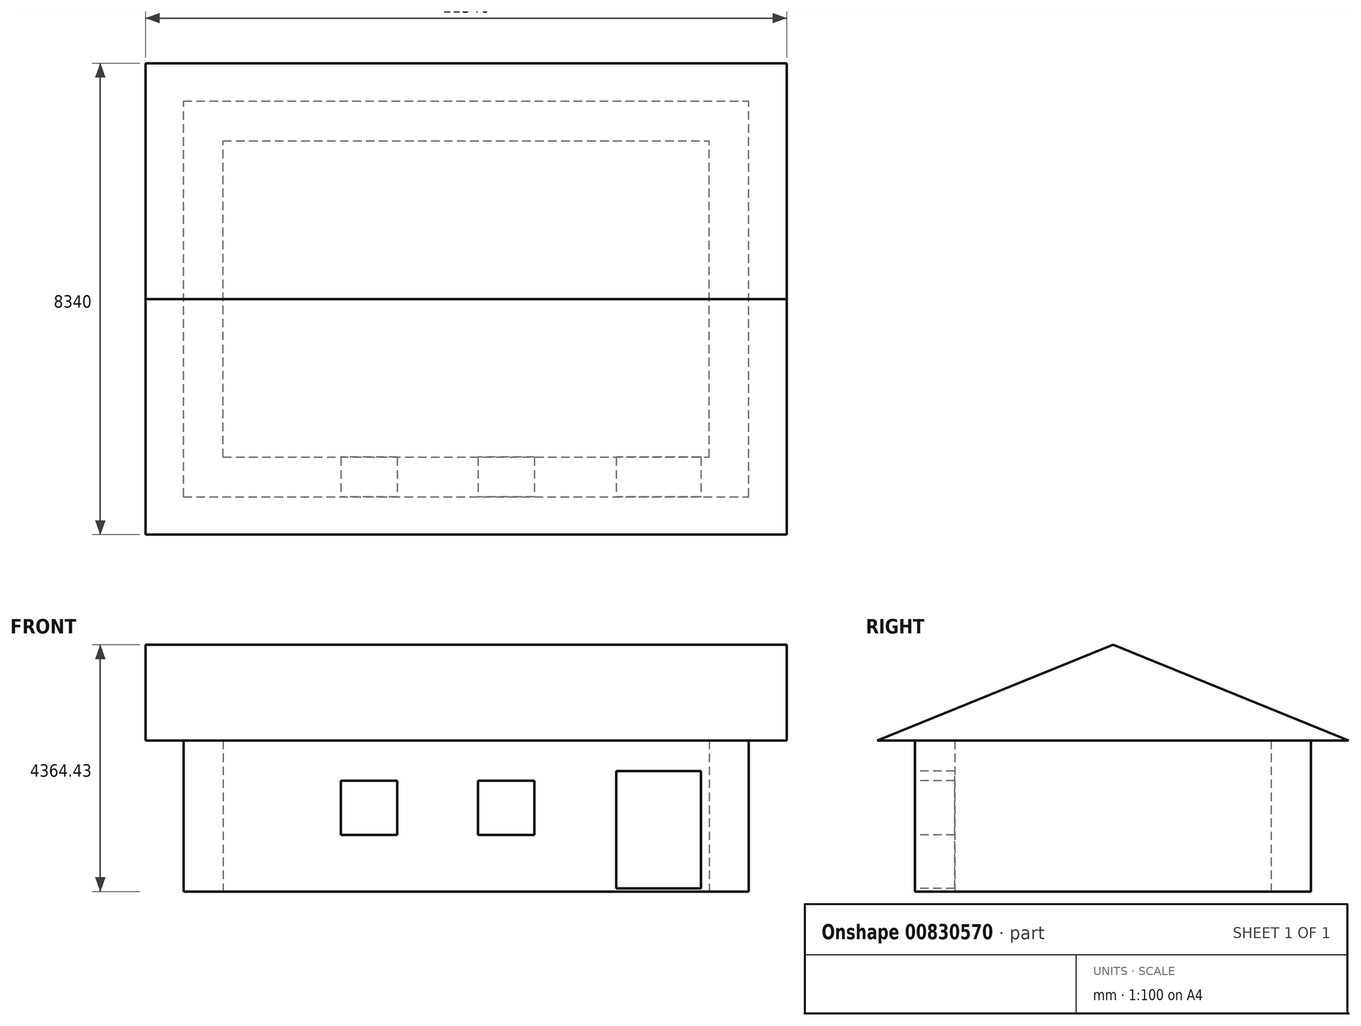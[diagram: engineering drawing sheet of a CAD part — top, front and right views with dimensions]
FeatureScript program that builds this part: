
annotation { "Feature Type Name" : "Feature", "Feature Type Description" : "" }
export const myFeature = defineFeature(function(context is Context, id is Id, definition is map)
    precondition{}
    {
        {
            var Q0;
            Q0=qCreatedBy(makeId("Top.planeOp"),FACE);
            var sketch = newSketch(context, id + "F0", { "sketchPlane" : qUnion([Q0])});
            skLineSegment(sketch, "E0.bottom", {"start": v(0, 0) * mm, "end": v(10000, 0) * mm});
            skLineSegment(sketch, "E0.top", {"start": v(0, 7000) * mm, "end": v(10000, 7000) * mm});
            skLineSegment(sketch, "E0.left", {"start": v(0, 0) * mm, "end": v(0, 7000) * mm});
            skLineSegment(sketch, "E0.right", {"start": v(10000, 0) * mm, "end": v(10000, 7000) * mm});
            skLineSegment(sketch, "E1.0", {"start": v(700, 6300) * mm, "end": v(9300, 6300) * mm});
            skLineSegment(sketch, "E1.1", {"start": v(700, 700) * mm, "end": v(700, 6300) * mm});
            skLineSegment(sketch, "E1.2", {"start": v(700, 700) * mm, "end": v(9300, 700) * mm});
            skLineSegment(sketch, "E1.3", {"start": v(9300, 700) * mm, "end": v(9300, 6300) * mm});
            skLineSegment(sketch, "E2.bottom", {"start": v(690.37, 700) * mm, "end": v(700, 700) * mm});
            skLineSegment(sketch, "E2.top", {"start": v(690.37, 0) * mm, "end": v(700, 0) * mm});
            skSolve(sketch);
        }
        {
            var Q0;
            Q0=makeQuery(id+"F0.imprint","IMPRINT",FACE,{"disambiguationData":[TD([[makeQuery(id+"F0.imprint","IMPRINT",EDGE,{"derivedFrom":sQuery(id+"F0.wireOp",EDGE,"E0.bottom")}),1.0]])]});
            extrude(context, id + "F1", {"entities" : qUnion([Q0]), "depth" : 2670 * mm, "offsetDistance" : 25 * mm});
        }
        {
            var Q0;
            Q0=makeQuery(id+"F1.opExtrude","SWEPT_FACE",FACE,{"disambiguationData":[OSD([sQuery(id+"F0.wireOp",EDGE,"E0.bottom"),sQuery(id+"F0.wireOp",EDGE,"E2.top")])]});
            var sketch = newSketch(context, id + "F2", { "sketchPlane" : qUnion([Q0])});
            skLineSegment(sketch, "E3.bottom", {"start": v(9153.14, 54.94) * mm, "end": v(7653.14, 54.94) * mm});
            skLineSegment(sketch, "E3.top", {"start": v(9153.14, 2131.26) * mm, "end": v(7653.14, 2131.26) * mm});
            skLineSegment(sketch, "E3.left", {"start": v(9153.14, 54.94) * mm, "end": v(9153.14, 2131.26) * mm});
            skLineSegment(sketch, "E3.right", {"start": v(7653.14, 54.94) * mm, "end": v(7653.14, 2131.26) * mm});
            skLineSegment(sketch, "E4.bottom", {"start": v(6207.25, 1000) * mm, "end": v(5207.25, 1000) * mm});
            skLineSegment(sketch, "E4.top", {"start": v(6207.25, 1960) * mm, "end": v(5207.25, 1960) * mm});
            skLineSegment(sketch, "E4.left", {"start": v(6207.25, 1000) * mm, "end": v(6207.25, 1960) * mm});
            skLineSegment(sketch, "E4.right", {"start": v(5207.25, 1000) * mm, "end": v(5207.25, 1960) * mm});
            skLineSegment(sketch, "E5.bottom", {"start": v(3783.6, 1000) * mm, "end": v(2783.6, 1000) * mm});
            skLineSegment(sketch, "E5.top", {"start": v(3783.6, 1960) * mm, "end": v(2783.6, 1960) * mm});
            skLineSegment(sketch, "E5.left", {"start": v(3783.6, 1000) * mm, "end": v(3783.6, 1960) * mm});
            skLineSegment(sketch, "E5.right", {"start": v(2783.6, 1000) * mm, "end": v(2783.6, 1960) * mm});
            skSolve(sketch);
        }
        {
            var Q0;
            {var subQ0=sQuery(id+"F2.wireOp",EDGE,"E3.bottom");Q0=makeQuery(id+"F2.imprint","IMPRINT",FACE,{"disambiguationData":[TD([[makeQuery(id+"F2.imprint","IMPRINT",EDGE,{"derivedFrom":subQ0}),-1.0]])]});}
            var Q1;
            Q1=makeQuery(id+"F2.imprint","IMPRINT",FACE,{"disambiguationData":[TD([[makeQuery(id+"F2.imprint","IMPRINT",EDGE,{"derivedFrom":sQuery(id+"F2.wireOp",EDGE,"E4.bottom")}),-1.0]])]});
            var Q2;
            Q2=makeQuery(id+"F2.imprint","IMPRINT",FACE,{"disambiguationData":[TD([[makeQuery(id+"F2.imprint","IMPRINT",EDGE,{"derivedFrom":sQuery(id+"F2.wireOp",EDGE,"E5.bottom")}),-1.0]])]});
            extrude(context, id + "F3", {"entities" : qUnion([Q0, Q1, Q2]), "operationType" : NewBodyOperationType.REMOVE, "endBound" : BoundingType.UP_TO_NEXT, "oppositeDirection" : true, "depth" : 1450 * mm, "offsetDistance" : 25 * mm});
        }
        {
            var Q0;
            Q0=makeQuery(id+"F1.opExtrude","SWEPT_FACE",FACE,{"disambiguationData":[OSD([sQuery(id+"F0.wireOp",EDGE,"E0.left")])]});
            var sketch = newSketch(context, id + "F4", { "sketchPlane" : qUnion([Q0])});
            skLineSegment(sketch, "E6", {"start": v(-7670, 2670) * mm, "end": v(670, 2670) * mm});
            skLineSegment(sketch, "E7", {"start": v(670, 2670) * mm, "end": v(-3500, 4364.43) * mm});
            skPoint(sketch, "E7.endSnap0", {"position": v(-3500, 2670) * mm});
            skLineSegment(sketch, "E8", {"start": v(-3500, 4364.43) * mm, "end": v(-7670, 2670) * mm});
            skSolve(sketch);
        }
        {
            var Q0;
            {var subQ0=sQuery(id+"F4.wireOp",EDGE,"E7");Q0=makeQuery(id+"F4.imprint","IMPRINT",FACE,{"disambiguationData":[TD([[makeQuery(id+"F4.imprint","IMPRINT",EDGE,{"derivedFrom":subQ0}),1.0]])]});}
            extrude(context, id + "F5", {"entities" : qUnion([Q0]), "operationType" : NewBodyOperationType.ADD, "depth" : 670 * mm, "offsetDistance" : 25 * mm, "hasSecondDirection" : true, "secondDirectionOppositeDirection" : true, "secondDirectionDepth" : 10670 * mm});
        }
    });
